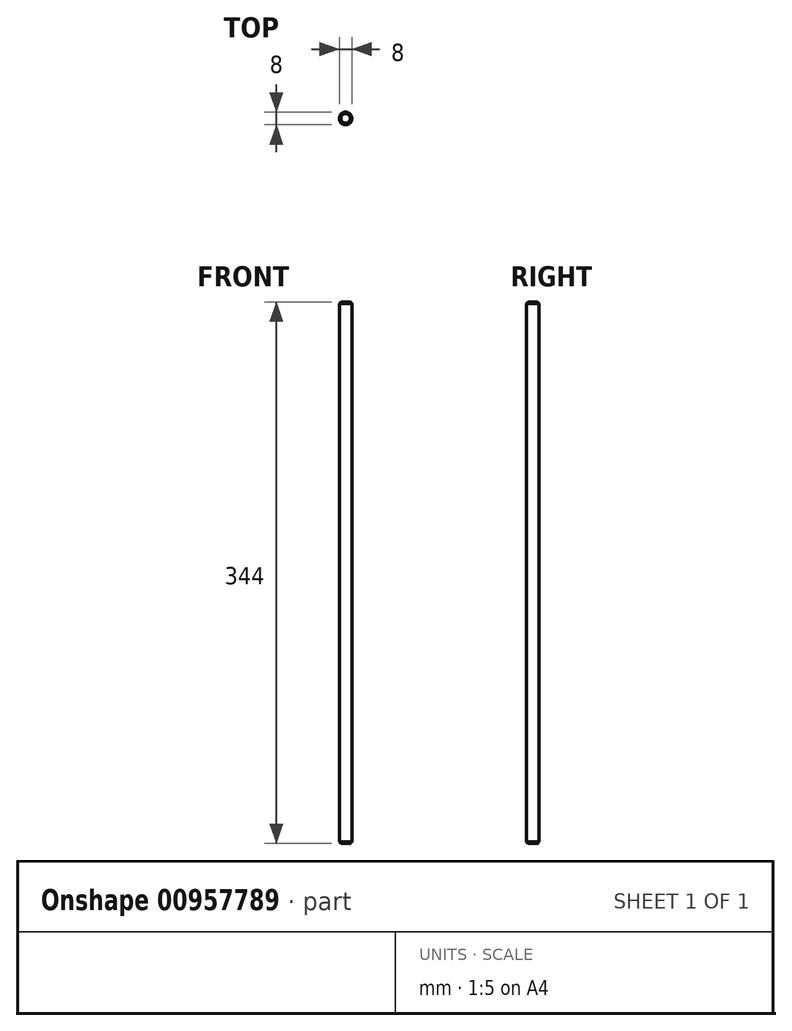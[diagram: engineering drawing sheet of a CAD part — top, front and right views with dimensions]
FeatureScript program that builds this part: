
annotation { "Feature Type Name" : "Feature", "Feature Type Description" : "" }
export const myFeature = defineFeature(function(context is Context, id is Id, definition is map)
    precondition{}
    {
        {
            var Q0;
            Q0=qCreatedBy(makeId("Top.planeOp"),FACE);
            var sketch = newSketch(context, id + "F0", { "sketchPlane" : qUnion([Q0])});
            skCircle(sketch, "E0", {"center": v(0, 0) * mm, "radius": 4 * mm});
            skSolve(sketch);
        }
        {
            var Q0;
            Q0=qSketchRegion(id+"F0",true);
            extrude(context, id + "F1", {"entities" : qUnion([Q0]), "depth" : 344 * mm, "offsetDistance" : 25 * mm});
        }
        {
            var Q0;
            Q0=makeQuery(id+"F1.opExtrude","CAP_EDGE",EDGE,{"disambiguationData":[OSD([sQuery(id+"F0.wireOp",EDGE,"E0")])],"isStart":true});
            var Q1;
            Q1=makeQuery(id+"F1.opExtrude","CAP_EDGE",EDGE,{"disambiguationData":[OSD([sQuery(id+"F0.wireOp",EDGE,"E0")])],"isStart":false});
            chamfer(context, id + "F2", {"entities" : qUnion([Q0, Q1]), "width" : 1 * mm, "tangentPropagation" : true});
        }
    });
